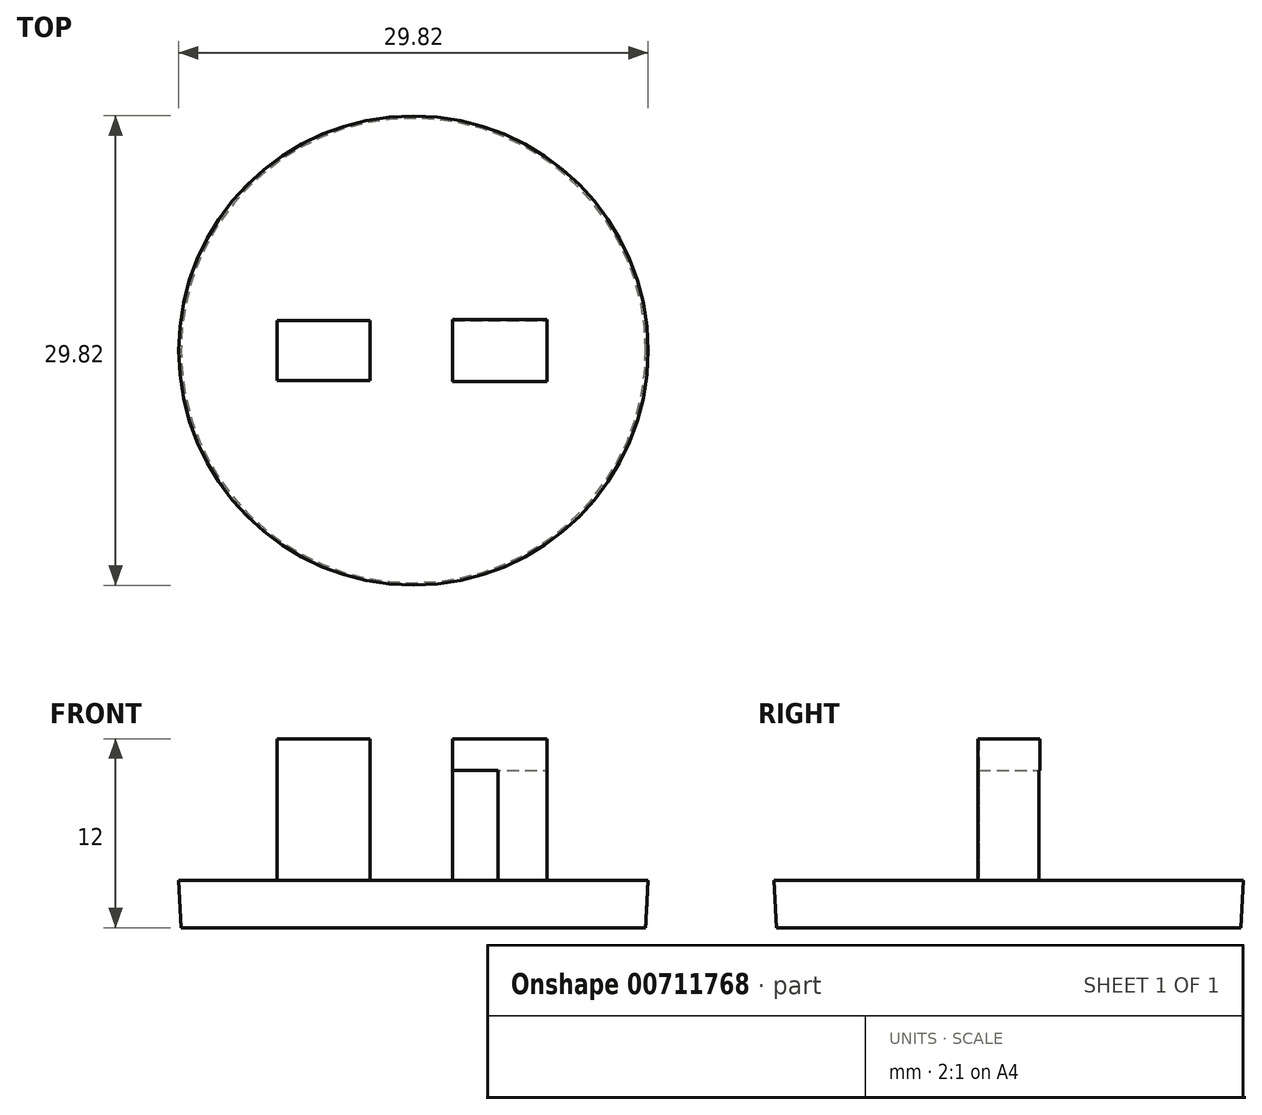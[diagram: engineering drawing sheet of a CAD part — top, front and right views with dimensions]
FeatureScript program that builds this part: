
annotation { "Feature Type Name" : "Feature", "Feature Type Description" : "" }
export const myFeature = defineFeature(function(context is Context, id is Id, definition is map)
    precondition{}
    {
        {
            var Q0;
            Q0=qCreatedBy(makeId("Top.planeOp"),FACE);
            var sketch = newSketch(context, id + "F0", { "sketchPlane" : qUnion([Q0])});
            skCircle(sketch, "E0", {"center": v(0, 0) * mm, "radius": 14.75 * mm});
            skSolve(sketch);
        }
        {
            var Q0;
            Q0=qSketchRegion(id+"F0",true);
            extrude(context, id + "F1", {"entities" : qUnion([Q0]), "depth" : 3 * mm, "offsetDistance" : 25.4 * mm, "hasDraft" : true, "draftAngle" : 3 * degree});
        }
        {
            var Q0;
            Q0=makeQuery(id+"F1.opExtrude","CAP_FACE",FACE,{"disambiguationData":[OSD([sQuery(id+"F0.wireOp",EDGE,"E0")])],"isStart":false});
            var sketch = newSketch(context, id + "F2", { "sketchPlane" : qUnion([Q0])});
            skLineSegment(sketch, "E1.bottom", {"start": v(-2.74, 1.9) * mm, "end": v(-5.55, 1.9) * mm});
            skLineSegment(sketch, "E1.top", {"start": v(-2.74, -1.9) * mm, "end": v(-5.55, -1.9) * mm});
            skLineSegment(sketch, "E1.left", {"start": v(-2.74, 1.9) * mm, "end": v(-2.74, -1.9) * mm});
            skLineSegment(sketch, "E1.right", {"start": v(-5.55, 1.9) * mm, "end": v(-5.55, -1.9) * mm});
            skPoint(sketch, "E1.middle", {"position": v(-4.15, 0) * mm});
            skLineSegment(sketch, "E2.bottom", {"start": v(2.48, 1.9) * mm, "end": v(5.37, 1.9) * mm});
            skLineSegment(sketch, "E2.top", {"start": v(2.48, -1.9) * mm, "end": v(5.37, -1.9) * mm});
            skLineSegment(sketch, "E2.left", {"start": v(2.48, 1.9) * mm, "end": v(2.48, -1.9) * mm});
            skLineSegment(sketch, "E2.right", {"start": v(5.37, 1.9) * mm, "end": v(5.37, -1.9) * mm});
            skPoint(sketch, "E2.middle", {"position": v(3.93, 0) * mm});
            skSolve(sketch);
        }
        {
            var Q0;
            Q0=qSketchRegion(id+"F2",true);
            extrude(context, id + "F3", {"entities" : qUnion([Q0]), "operationType" : NewBodyOperationType.ADD, "depth" : 7 * mm, "offsetDistance" : 25.4 * mm});
        }
        {
            var Q0;
            Q0=makeQuery(id+"F3.opExtrude","CAP_FACE",FACE,{"disambiguationData":[OSD([sQuery(id+"F2.wireOp",EDGE,"E1.bottom"),sQuery(id+"F2.wireOp",EDGE,"E1.top"),sQuery(id+"F2.wireOp",EDGE,"E1.left"),sQuery(id+"F2.wireOp",EDGE,"E1.right")])],"isStart":false});
            var sketch = newSketch(context, id + "F4", { "sketchPlane" : qUnion([Q0])});
            skLineSegment(sketch, "E3.bottom", {"start": v(-2.74, 1.9) * mm, "end": v(-8.66, 1.9) * mm});
            skLineSegment(sketch, "E3.top", {"start": v(-2.74, -1.9) * mm, "end": v(-8.66, -1.9) * mm});
            skLineSegment(sketch, "E3.left", {"start": v(-2.74, 1.9) * mm, "end": v(-2.74, -1.9) * mm});
            skLineSegment(sketch, "E3.right", {"start": v(-8.66, 1.9) * mm, "end": v(-8.66, -1.9) * mm});
            skLineSegment(sketch, "E4.bottom", {"start": v(2.5, -1.97) * mm, "end": v(8.5, -1.97) * mm});
            skLineSegment(sketch, "E4.top", {"start": v(2.5, 1.96) * mm, "end": v(8.5, 1.96) * mm});
            skLineSegment(sketch, "E4.left", {"start": v(2.5, -1.97) * mm, "end": v(2.5, 1.96) * mm});
            skLineSegment(sketch, "E4.right", {"start": v(8.5, -1.97) * mm, "end": v(8.5, 1.96) * mm});
            skSolve(sketch);
        }
        {
            var Q0;
            Q0=qSketchRegion(id+"F4",true);
            extrude(context, id + "F5", {"entities" : qUnion([Q0]), "operationType" : NewBodyOperationType.ADD, "depth" : 2 * mm, "offsetDistance" : 25 * mm});
        }
        {
            var Q0;
            Q0=makeQuery(id+"F5.opExtrude","CAP_FACE",FACE,{"disambiguationData":[OSD([sQuery(id+"F4.wireOp",EDGE,"E4.bottom"),sQuery(id+"F4.wireOp",EDGE,"E4.top"),sQuery(id+"F4.wireOp",EDGE,"E4.left"),sQuery(id+"F4.wireOp",EDGE,"E4.right")])],"isStart":true});
            var sketch = newSketch(context, id + "F6", { "sketchPlane" : qUnion([Q0])});
            skLineSegment(sketch, "E5.bottom", {"start": v(5.37, -1.9) * mm, "end": v(8.5, -1.9) * mm});
            skLineSegment(sketch, "E5.top", {"start": v(5.37, 1.97) * mm, "end": v(8.5, 1.97) * mm});
            skLineSegment(sketch, "E5.left", {"start": v(5.37, -1.9) * mm, "end": v(5.37, 1.97) * mm});
            skLineSegment(sketch, "E5.right", {"start": v(8.5, -1.9) * mm, "end": v(8.5, 1.97) * mm});
            skLineSegment(sketch, "E6.bottom", {"start": v(8.5, 1.97) * mm, "end": v(5.37, 1.97) * mm});
            skLineSegment(sketch, "E6.top", {"start": v(8.5, -1.9) * mm, "end": v(5.37, -1.9) * mm});
            skLineSegment(sketch, "E6.left", {"start": v(8.5, 1.97) * mm, "end": v(8.5, -1.9) * mm});
            skLineSegment(sketch, "E6.right", {"start": v(5.37, 1.97) * mm, "end": v(5.37, -1.9) * mm});
            skSolve(sketch);
        }
        {
            var Q0;
            Q0 = qSketchRegion(id + "F6", true);
            extrude(context, id + "F7", {"entities" : qUnion([Q0]), "operationType" : NewBodyOperationType.ADD, "depth" : 7 * mm, "offsetDistance" : 25 * mm});
        }
        {
            var Q0;
            Q0=makeQuery(id+"F5.opExtrude","CAP_FACE",FACE,{"disambiguationData":[OSD([sQuery(id+"F4.wireOp",EDGE,"E3.bottom"),sQuery(id+"F4.wireOp",EDGE,"E3.top"),sQuery(id+"F4.wireOp",EDGE,"E3.left"),sQuery(id+"F4.wireOp",EDGE,"E3.right")])],"isStart":true});
            var sketch = newSketch(context, id + "F8", { "sketchPlane" : qUnion([Q0])});
            skLineSegment(sketch, "E7.bottom", {"start": v(-8.66, -1.9) * mm, "end": v(-5.55, -1.9) * mm});
            skLineSegment(sketch, "E7.top", {"start": v(-8.66, 1.9) * mm, "end": v(-5.55, 1.9) * mm});
            skLineSegment(sketch, "E7.left", {"start": v(-8.66, -1.9) * mm, "end": v(-8.66, 1.9) * mm});
            skLineSegment(sketch, "E7.right", {"start": v(-5.55, -1.9) * mm, "end": v(-5.55, 1.9) * mm});
            skSolve(sketch);
        }
        {
            var Q0;
            Q0 = qSketchRegion(id + "F8", true);
            extrude(context, id + "F9", {"entities" : qUnion([Q0]), "operationType" : NewBodyOperationType.ADD, "depth" : 7 * mm, "offsetDistance" : 25 * mm});
        }
    });
